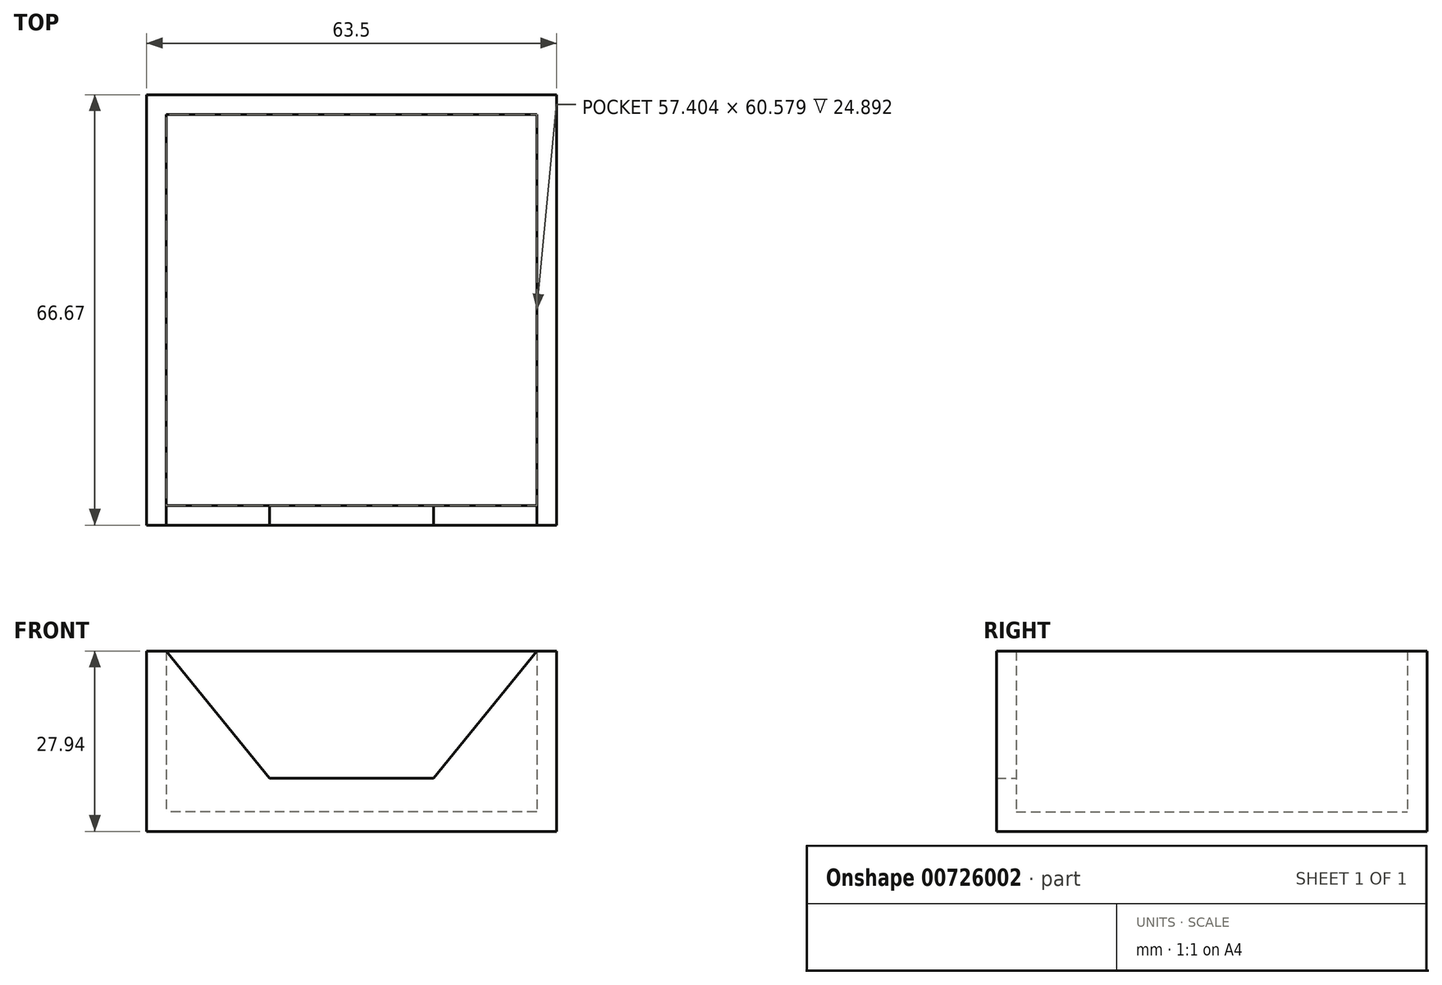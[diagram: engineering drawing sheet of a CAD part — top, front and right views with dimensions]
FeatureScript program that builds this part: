
annotation { "Feature Type Name" : "Feature", "Feature Type Description" : "" }
export const myFeature = defineFeature(function(context is Context, id is Id, definition is map)
    precondition{}
    {
        {
            var Q0;
            Q0=qCreatedBy(makeId("Front.planeOp"),FACE);
            var sketch = newSketch(context, id + "F0", { "sketchPlane" : qUnion([Q0])});
            skLineSegment(sketch, "E0.bottom", {"start": v(31.75, 13.97) * mm, "end": v(-31.75, 13.97) * mm});
            skLineSegment(sketch, "E0.top", {"start": v(31.75, -13.97) * mm, "end": v(-31.75, -13.97) * mm});
            skLineSegment(sketch, "E0.left", {"start": v(31.75, 13.97) * mm, "end": v(31.75, -13.97) * mm});
            skLineSegment(sketch, "E0.right", {"start": v(-31.75, 13.97) * mm, "end": v(-31.75, -13.97) * mm});
            skPoint(sketch, "E0.middle", {"position": v(0, 0) * mm});
            skSolve(sketch);
        }
        {
            var Q0;
            Q0=makeQuery(id+"F0.imprint","IMPRINT",FACE,{"disambiguationData":[TD([[makeQuery(id+"F0.imprint","IMPRINT",EDGE,{"derivedFrom":sQuery(id+"F0.wireOp",EDGE,"E0.bottom")}),1.0]])]});
            extrude(context, id + "F1", {"entities" : qUnion([Q0]), "depth" : 66.67 * mm, "offsetDistance" : 25.4 * mm});
        }
        {
            var Q0;
            Q0=makeQuery(id+"F1.opExtrude","SWEPT_FACE",FACE,{"disambiguationData":[OSD([sQuery(id+"F0.wireOp",EDGE,"E0.bottom")])]});
            shell(context, id + "F2", {"entities" : qUnion([Q0]), "thickness" : 3.05 * mm});
        }
        {
            var Q0;
            {var subQ0=sQuery(id+"F0.wireOp",EDGE,"E0.right");var subQ1=sQuery(id+"F0.wireOp",EDGE,"E0.left");var subQ2=sQuery(id+"F0.wireOp",EDGE,"E0.top");var subQ3=sQuery(id+"F0.wireOp",EDGE,"E0.bottom");Q0=makeQuery(id+"F2.opShell","OFFSET_FACE",FACE,{"disambiguationData":[OSD([subQ3,subQ2,subQ1,subQ0]),TDD([makeQuery(id+"F1.opExtrude","CAP_FACE",FACE,{"disambiguationData":[OSD([subQ3,subQ2,subQ1,subQ0])],"isStart":false})])]});}
            var sketch = newSketch(context, id + "F3", { "sketchPlane" : qUnion([Q0])});
            skLineSegment(sketch, "E1", {"start": v(28.7, 13.97) * mm, "end": v(12.7, -5.76) * mm});
            skLineSegment(sketch, "E2", {"start": v(12.7, -5.76) * mm, "end": v(0, -5.76) * mm});
            skLineSegment(sketch, "E3", {"start": v(0, -5.76) * mm, "end": v(-12.7, -5.76) * mm});
            skLineSegment(sketch, "E4", {"start": v(-12.7, -5.76) * mm, "end": v(-28.7, 13.97) * mm});
            skSolve(sketch);
        }
        {
            var Q0;
            Q0=makeQuery(id+"F3.imprint","IMPRINT",FACE,{"disambiguationData":[TD([[makeQuery(id+"F3.imprint","IMPRINT",EDGE,{"derivedFrom":sQuery(id+"F3.wireOp",EDGE,"E1")}),-1.0]])]});
            extrude(context, id + "F4", {"entities" : qUnion([Q0]), "operationType" : NewBodyOperationType.REMOVE, "oppositeDirection" : true, "depth" : 25.4 * mm, "offsetDistance" : 25.4 * mm});
        }
    });
